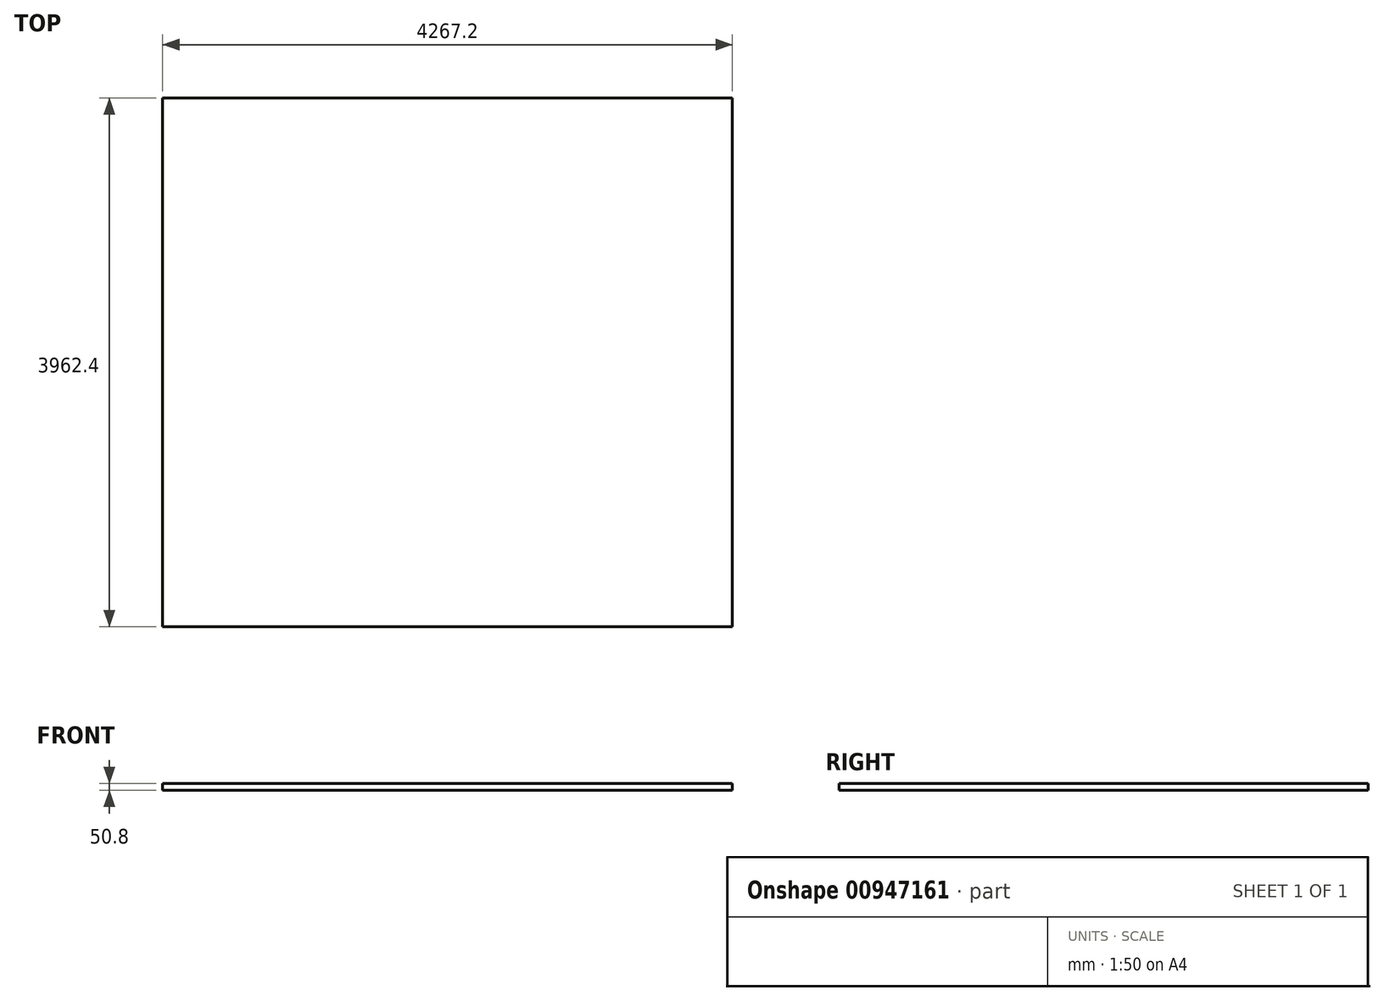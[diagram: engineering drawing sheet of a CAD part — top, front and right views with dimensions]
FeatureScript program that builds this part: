
annotation { "Feature Type Name" : "Feature", "Feature Type Description" : "" }
export const myFeature = defineFeature(function(context is Context, id is Id, definition is map)
    precondition{}
    {
        {
            var Q0;
            Q0=qCreatedBy(makeId("Top.planeOp"),FACE);
            var sketch = newSketch(context, id + "F0", { "sketchPlane" : qUnion([Q0])});
            skLineSegment(sketch, "E0.bottom", {"start": v(0, 0) * mm, "end": v(4267.2, 0) * mm});
            skLineSegment(sketch, "E0.top", {"start": v(0, 3962.4) * mm, "end": v(4267.2, 3962.4) * mm});
            skLineSegment(sketch, "E0.left", {"start": v(0, 0) * mm, "end": v(0, 3962.4) * mm});
            skLineSegment(sketch, "E0.right", {"start": v(4267.2, 0) * mm, "end": v(4267.2, 3962.4) * mm});
            skSolve(sketch);
        }
        {
            var Q0;
            Q0 = qSketchRegion(id + "F0", true);
            extrude(context, id + "F1", {"entities" : qUnion([Q0]), "depth" : 50.8 * mm, "offsetDistance" : 25.4 * mm});
        }
    });
